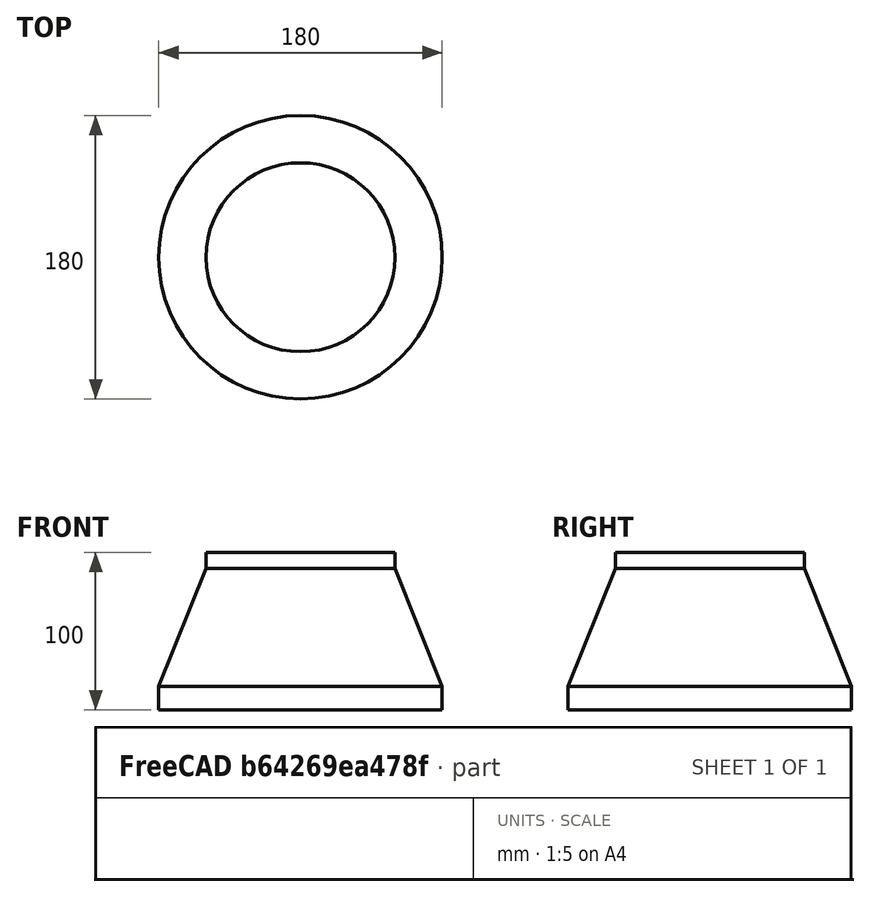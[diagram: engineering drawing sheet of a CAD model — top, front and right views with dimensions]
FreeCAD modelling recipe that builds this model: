
FCSTD DOCUMENT  (FreeCAD 0.19R)
Label: link_0
License: All rights reserved
LicenseURL: http://en.wikipedia.org/wiki/All_rights_reserved
objects: Sketcher::SketchObject×1, PartDesign::Revolution×1, PartDesign::Body×1
note: 4 computed .brp shape members not serialized (recipe doc carries the construction recipe); baked Part::Feature solids carry a one-line shape summary decoded from their .brp

FEATURE [Sketcher::SketchObject] Sketch
  FullyConstrained = false
  MapMode = 5
  Placement = pos=(0,0,0) rot=(1,0,0;1.5708rad)
  Support = -> [XZ_Plane]
  sketch-geometry (6):
    g0: LineSegment StartX=1e-16 StartY=50 StartZ=0 EndX=0 EndY=-50 EndZ=0
    g1: LineSegment StartX=1e-16 StartY=50 StartZ=0 EndX=60 EndY=50 EndZ=0
    g2: LineSegment StartX=60 StartY=50 StartZ=0 EndX=60 EndY=40 EndZ=0
    g3: LineSegment StartX=0 StartY=-50 StartZ=0 EndX=90 EndY=-50 EndZ=0
    g4: LineSegment StartX=90 StartY=-50 StartZ=0 EndX=90 EndY=-35 EndZ=0
    g5: LineSegment StartX=90 StartY=-35 StartZ=0 EndX=60 EndY=40 EndZ=0
  constraints (17):
    c: Symmetric(g0,g0,g-1)
    c: PointOnObject(g0,g-2)
    c: DistanceY(g0,g0) = 100
    c: Coincident(g1,g0)
    c: Horizontal(g1)
    c: DistanceX(g1,g1) = 60
    c: Coincident(g2,g1)
    c: Vertical(g2)
    c: Horizontal(g3)
    c: Vertical(g4)
    c: Coincident(g5,g2)
    c: DistanceX(g3,g3) = 90
    c: Coincident(g3,g0)
    c: Coincident(g4,g3)
    c: Coincident(g5,g4)
    c: DistanceY(g2,g2) = 10
    c: DistanceY(g4,g4) = 15
FEATURE [PartDesign::Revolution] Revolution
  AllowMultiFace = false
  Angle = 360
  Axis = (0,2e-16,1)
  Base = (0,0,0)
  Placement = pos=(0,0,0) rot=(1,0,0;1.5708rad)
  Profile = -> Sketch
  ReferenceAxis = -> Sketch [V_Axis]
  Reversed = true
FEATURE [PartDesign::Body] Body
  Group = -> [Sketch,Revolution]
  Origin = -> Origin
  Tip = -> Revolution
